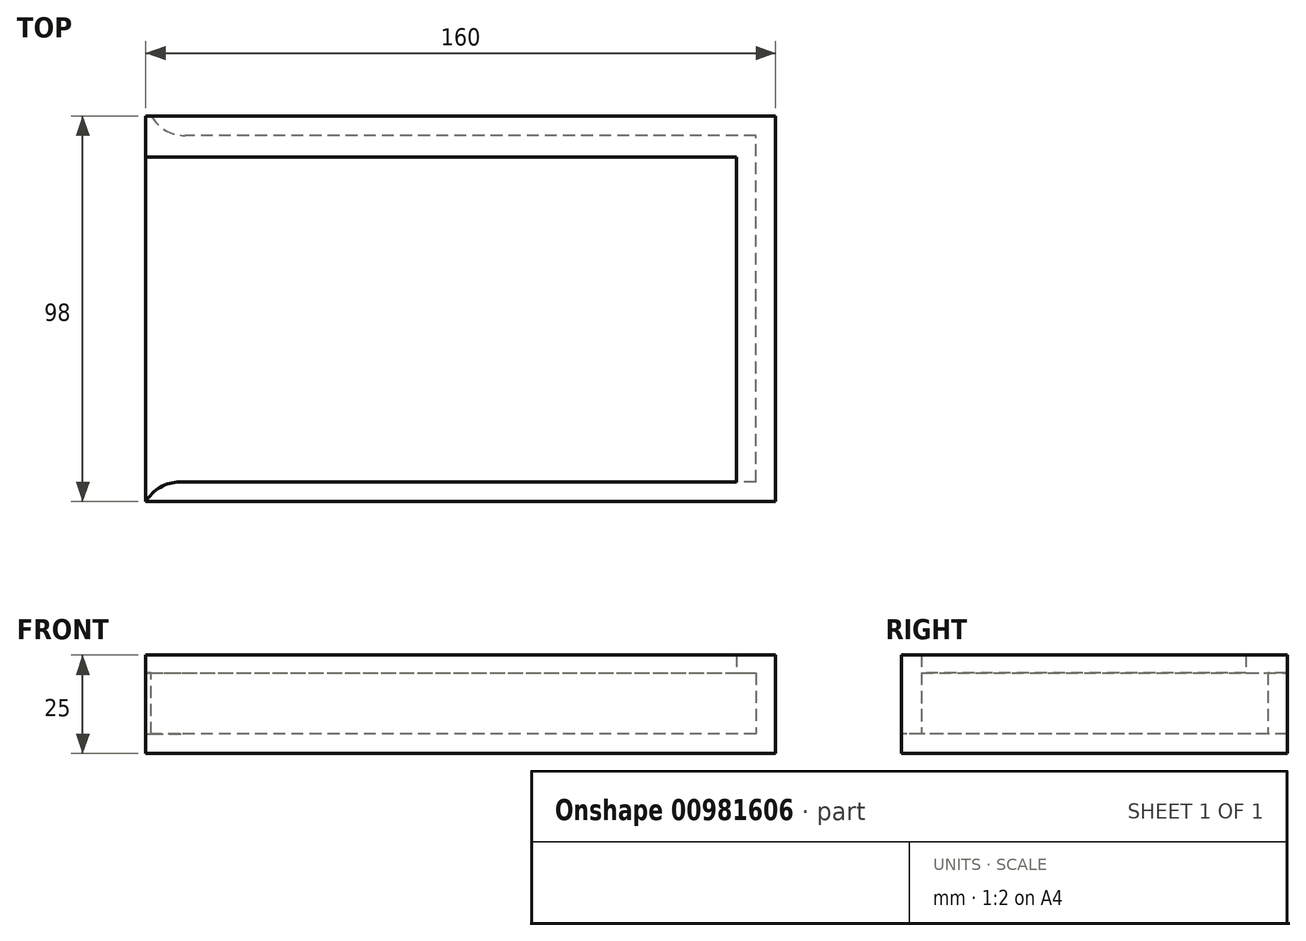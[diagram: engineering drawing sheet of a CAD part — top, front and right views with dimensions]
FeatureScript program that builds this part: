
annotation { "Feature Type Name" : "Feature", "Feature Type Description" : "" }
export const myFeature = defineFeature(function(context is Context, id is Id, definition is map)
    precondition{}
    {
        {
            var Q0;
            Q0=qCreatedBy(makeId("Top.planeOp"),FACE);
            var sketch = newSketch(context, id + "F0", { "sketchPlane" : qUnion([Q0])});
            skLineSegment(sketch, "E0.bottom", {"start": v(80, 44) * mm, "end": v(-80, 44) * mm});
            skLineSegment(sketch, "E0.top", {"start": v(80, -44) * mm, "end": v(-80, -44) * mm});
            skLineSegment(sketch, "E0.left", {"start": v(80, 44) * mm, "end": v(80, -44) * mm});
            skLineSegment(sketch, "E0.right", {"start": v(-80, 44) * mm, "end": v(-80, -44) * mm});
            skPoint(sketch, "E0.middle", {"position": v(0, 0) * mm});
            skLineSegment(sketch, "E1", {"start": v(80, 44) * mm, "end": v(75, 44) * mm, "construction": true});
            skLineSegment(sketch, "E2", {"start": v(75, 44) * mm, "end": v(75, -44) * mm});
            skLineSegment(sketch, "E3", {"start": v(80, 44) * mm, "end": v(80, 49) * mm});
            skLineSegment(sketch, "E4", {"start": v(80, 49) * mm, "end": v(-80, 49) * mm});
            skLineSegment(sketch, "E5", {"start": v(-80, 44) * mm, "end": v(-80, 49) * mm});
            skLineSegment(sketch, "E6.MirrorCS", {"start": v(80, -49) * mm, "end": v(-80, -49) * mm});
            skLineSegment(sketch, "E7.MirrorCS", {"start": v(80, -44) * mm, "end": v(80, -49) * mm});
            skLineSegment(sketch, "E8.MirrorCS", {"start": v(-80, -44) * mm, "end": v(-80, -49) * mm});
            skSolve(sketch);
        }
        {
            var Q0;
            {var subQ0=sQuery(id+"F0.wireOp",EDGE,"E0.right");Q0=makeQuery(id+"F0.imprint","IMPRINT",FACE,{"disambiguationData":[TD([[makeQuery(id+"F0.imprint","IMPRINT",EDGE,{"derivedFrom":subQ0}),1.0]])]});}
            extrude(context, id + "F1", {"entities" : qUnion([Q0]), "depth" : 5 * mm, "offsetDistance" : 25 * mm});
        }
        {
            var Q0;
            {var subQ0=sQuery(id+"F0.wireOp",EDGE,"E3");Q0=makeQuery(id+"F0.imprint","IMPRINT",FACE,{"disambiguationData":[TD([[makeQuery(id+"F0.imprint","IMPRINT",EDGE,{"derivedFrom":subQ0}),1.0]])]});}
            var Q1;
            {var subQ0=sQuery(id+"F0.wireOp",EDGE,"E0.left");Q1=makeQuery(id+"F0.imprint","IMPRINT",FACE,{"disambiguationData":[TD([[makeQuery(id+"F0.imprint","IMPRINT",EDGE,{"derivedFrom":subQ0}),-1.0]])]});}
            var Q2;
            Q2=makeQuery(id+"F0.imprint","IMPRINT",FACE,{"disambiguationData":[TD([[makeQuery(id+"F0.imprint","IMPRINT",EDGE,{"derivedFrom":sQuery(id+"F0.wireOp",EDGE,"E6.MirrorCS")}),-1.0]])]});
            extrude(context, id + "F2", {"entities" : qUnion([Q0, Q1, Q2]), "operationType" : NewBodyOperationType.ADD, "depth" : 25 * mm, "offsetDistance" : 25 * mm});
        }
        {
            var Q0;
            Q0=makeQuery(id+"F2.opExtrude","SWEPT_FACE",FACE,{"disambiguationData":[OSD([sQuery(id+"F0.wireOp",EDGE,"E0.bottom")])]});
            var sketch = newSketch(context, id + "F3", { "sketchPlane" : qUnion([Q0])});
            skLineSegment(sketch, "E9", {"start": v(-80, 25) * mm, "end": v(-80, 20.5) * mm, "construction": true});
            skLineSegment(sketch, "E10", {"start": v(-80, 20.5) * mm, "end": v(75, 20.5) * mm});
            skSolve(sketch);
        }
        {
            var Q0;
            {var subQ0=sQuery(id+"F3.wireOp",EDGE,"E10");Q0=makeQuery(id+"F3.imprint","IMPRINT",FACE,{"disambiguationData":[TD([[makeQuery(id+"F3.imprint","IMPRINT",EDGE,{"derivedFrom":subQ0}),1.0]])]});}
            extrude(context, id + "F4", {"entities" : qUnion([Q0]), "operationType" : NewBodyOperationType.ADD, "depth" : 5.5 * mm, "offsetDistance" : 25 * mm});
        }
        {
            var Q0;
            Q0=makeQuery(id+"F2.opExtrude","SWEPT_FACE",FACE,{"disambiguationData":[OSD([sQuery(id+"F0.wireOp",EDGE,"E2")])]});
            var sketch = newSketch(context, id + "F5", { "sketchPlane" : qUnion([Q0])});
            skLineSegment(sketch, "E11", {"start": v(-38.5, 20.5) * mm, "end": v(44, 20.5) * mm});
            skSolve(sketch);
        }
        {
            var Q0;
            {var subQ0=sQuery(id+"F5.wireOp",EDGE,"E11");Q0=makeQuery(id+"F5.imprint","IMPRINT",FACE,{"disambiguationData":[TD([[makeQuery(id+"F5.imprint","IMPRINT",EDGE,{"derivedFrom":subQ0}),1.0]])]});}
            extrude(context, id + "F6", {"entities" : qUnion([Q0]), "operationType" : NewBodyOperationType.ADD, "depth" : 5 * mm, "offsetDistance" : 25 * mm});
        }
        {
            var Q0;
            Q0=makeQuery(id+"F2.opExtrude","SWEPT_EDGE",EDGE,{"disambiguationData":[OSD([sQuery(id+"F0.wireOp",EDGE,"E0.top"),sQuery(id+"F0.wireOp",EDGE,"E0.right"),sQuery(id+"F0.wireOp",EDGE,"E8.MirrorCS")])]});
            var Q1;
            Q1=makeQuery(id+"F2.opExtrude","SWEPT_EDGE",EDGE,{"disambiguationData":[OSD([sQuery(id+"F0.wireOp",EDGE,"E0.bottom"),sQuery(id+"F0.wireOp",EDGE,"E0.right"),sQuery(id+"F0.wireOp",EDGE,"E5")])]});
            fillet(context, id + "F7", {"entities" : qUnion([Q0, Q1]), "radius" : 10 * mm, "tangentPropagation" : true, "allowEdgeOverflow" : false});
        }
    });
